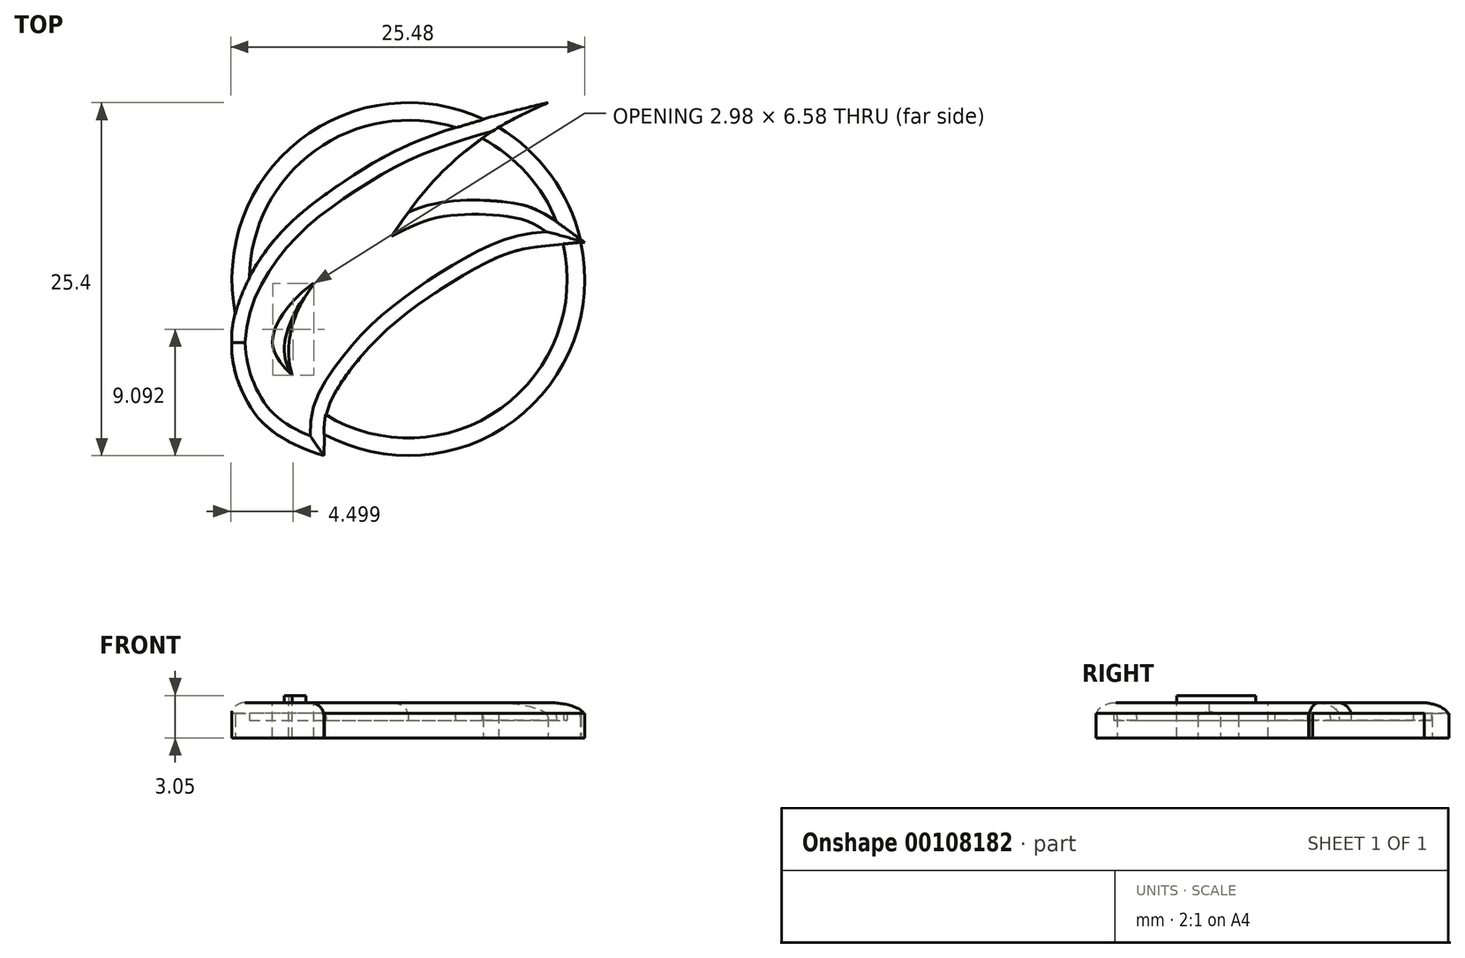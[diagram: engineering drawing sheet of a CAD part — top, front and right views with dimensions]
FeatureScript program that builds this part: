
annotation { "Feature Type Name" : "Feature", "Feature Type Description" : "" }
export const myFeature = defineFeature(function(context is Context, id is Id, definition is map)
    precondition{}
    {
        {
            var Q0;
            Q0=qCreatedBy(makeId("Top.planeOp"),FACE);
            var sketch = newSketch(context, id + "F0", { "sketchPlane" : qUnion([Q0])});
            skLineSegment(sketch, "E0.bottom", {"start": v(12.7, 12.7) * mm, "end": v(-12.7, 12.7) * mm});
            skLineSegment(sketch, "E0.top", {"start": v(12.7, -12.7) * mm, "end": v(-12.7, -12.7) * mm});
            skLineSegment(sketch, "E0.left", {"start": v(12.7, 12.7) * mm, "end": v(12.7, -12.7) * mm});
            skLineSegment(sketch, "E0.right", {"start": v(-12.7, 12.7) * mm, "end": v(-12.7, -12.7) * mm});
            skPoint(sketch, "E0.middle", {"position": v(0, 0) * mm});
            skFitSpline(sketch, "E1", {"points": [v(-6.08, -12.7) * mm, v(-11.49, -9) * mm, v(-12.7, -3.76) * mm, v(-9.57, 2.9) * mm, v(-4.09, 7.38) * mm, v(10.05, 12.7) * mm], "startDerivative": vector(-51.73, 16.39) * mm, "endDerivative": vector(97.1, 22.66) * mm});
            skFitSpline(sketch, "E2", {"points": [v(0, 4.8) * mm, v(6.97, 5.55) * mm, v(12.7, 2.64) * mm], "startDerivative": vector(12.66, 6.1) * mm, "endDerivative": vector(18.75, -14.7) * mm});
            skFitSpline(sketch, "E3", {"points": [v(-6.08, -12.7) * mm, v(-5.75, -9.17) * mm, v(-2.84, -4.93) * mm, v(1.65, -1.18) * mm, v(6.8, 1.73) * mm, v(12.7, 2.64) * mm], "startDerivative": vector(1.52, 34.14) * mm, "endDerivative": vector(48.68, 4.54) * mm});
            skFitSpline(sketch, "E4", {"points": [v(0, 4.8) * mm, v(4.64, 9.63) * mm, v(10.05, 12.7) * mm], "startDerivative": vector(11.2, 15.67) * mm, "endDerivative": vector(20.33, 9.14) * mm});
            skSolve(sketch);
        }
        {
            var Q0;
            {var subQ0=sQuery(id+"F0.wireOp",EDGE,"E1");var subQ1=sQuery(id+"F0.wireOp",EDGE,"E0.right");var subQ2=makeQuery(id+"F0.imprint","INTERSECT",VERTEX,{"disambiguationData":[OD(0.0)],"derivedFrom":[subQ1,subQ0]});Q0=makeQuery(id+"F0.imprint","IMPRINT",FACE,{"disambiguationData":[TD([[makeQuery(id+"F0.imprint","IMPRINT",EDGE,{"disambiguationData":[TD([[subQ2,-1.0]])],"derivedFrom":subQ1}),-1.0]])]});}
            var Q1;
            {var subQ0=sQuery(id+"F0.wireOp",EDGE,"c1Eb6WPf-WvlZ-wcMs-vn4g-5d7YpBRqAoRS");Q1=makeQuery(id+"F0.imprint","IMPRINT",FACE,{"disambiguationData":[TD([[makeQuery(id+"F0.imprint","IMPRINT",EDGE,{"derivedFrom":subQ0}),-1.0]])]});}
            var Q2;
            Q2=makeQuery(id+"F0.imprint","IMPRINT",FACE,{"disambiguationData":[TD([[makeQuery(id+"F0.imprint","IMPRINT",EDGE,{"derivedFrom":sQuery(id+"F0.wireOp",EDGE,"E2")}),-1.0]])]});
            extrude(context, id + "F1", {"entities" : qUnion([Q0, Q1, Q2]), "depth" : 2.54 * mm});
        }
        {
            var Q0;
            Q0=makeQuery(id+"F1.opExtrude","CAP_FACE",FACE,{"disambiguationData":[OSD([sQuery(id+"F0.wireOp",EDGE,"E1"),sQuery(id+"F0.wireOp",EDGE,"c1Eb6WPf-WvlZ-wcMs-vn4g-5d7YpBRqAoRS"),sQuery(id+"F0.wireOp",EDGE,"E2"),sQuery(id+"F0.wireOp",EDGE,"E3")])],"isStart":false});
            var sketch = newSketch(context, id + "F2", { "sketchPlane" : qUnion([Q0])});
            skFitSpline(sketch, "E5", {"points": [v(-6.8, -0.32) * mm, v(-9.75, -4.16) * mm, v(-8.37, -6.9) * mm], "startDerivative": vector(-5.92, -3.3) * mm, "endDerivative": vector(5.55, -5.41) * mm});
            skFitSpline(sketch, "E6", {"points": [v(-8.37, -6.9) * mm, v(-8.01, -2.38) * mm, v(-6.8, -0.32) * mm], "startDerivative": vector(-2.94, 9.89) * mm, "endDerivative": vector(4.93, 7.27) * mm});
            skSolve(sketch);
        }
        {
            var Q0;
            Q0=qCreatedBy(makeId("Top.planeOp"),FACE);
            var sketch = newSketch(context, id + "F3", { "sketchPlane" : qUnion([Q0])});
            skCircle(sketch, "E7", {"center": v(0, 0) * mm, "radius": 12.7 * mm});
            skSolve(sketch);
        }
        {
            var Q0;
            Q0 = qSketchRegion(id + "F3", true);
            extrude(context, id + "F4", {"entities" : qUnion([Q0]), "operationType" : NewBodyOperationType.ADD, "depth" : 1.27 * mm});
        }
        {
            var Q0;
            Q0 = qSketchRegion(id + "F2", true);
            extrude(context, id + "F5", {"entities" : qUnion([Q0]), "operationType" : NewBodyOperationType.REMOVE, "oppositeDirection" : true, "depth" : 25.4 * mm});
        }
        {
            var Q0;
            Q0=makeQuery(id+"F1.opExtrude","CAP_FACE",FACE,{"disambiguationData":[OSD([sQuery(id+"F0.wireOp",EDGE,"E1"),sQuery(id+"F0.wireOp",EDGE,"c1Eb6WPf-WvlZ-wcMs-vn4g-5d7YpBRqAoRS"),sQuery(id+"F0.wireOp",EDGE,"E2"),sQuery(id+"F0.wireOp",EDGE,"E3")])],"isStart":false});
            var sketch = newSketch(context, id + "F6", { "sketchPlane" : qUnion([Q0])});
            skFitSpline(sketch, "E8.0.0", {"points": [v(7.91, 12.7) * mm, v(4.26, 10.89) * mm, v(-2.84, 7.4) * mm, v(-8.76, 3.35) * mm, v(-14.41, -4.34) * mm, v(-9.73, -11.02) * mm, v(-6.67, -11.7) * mm, v(-3.5, -12.7) * mm]});
            skFitSpline(sketch, "E8.0.1", {"points": [v(-3.5, -12.7) * mm, v(-4.54, -10.95) * mm, v(-4.91, -10.68) * mm, v(-4.48, -6.55) * mm, v(-0.85, -3.27) * mm, v(6.87, 2.24) * mm, v(11.13, 6.28) * mm, v(12.7, 8.06) * mm]});
            skFitSpline(sketch, "E8.0.2", {"points": [v(12.7, 8.06) * mm, v(10.6, 7.69) * mm, v(6.36, 5.46) * mm, v(2.13, 3.93) * mm, v(0, 2.9) * mm]});
            skLineSegment(sketch, "E8.0.3", {"start": v(0, 4.8) * mm, "end": v(10.05, 12.7) * mm});
            skFitSpline(sketch, "E9.0", {"points": [v(-8.37, -6.9) * mm, v(-8.94, -5) * mm, v(-8.04, -2.15) * mm, v(-7.48, -1.34) * mm, v(-6.8, -0.32) * mm]});
            skFitSpline(sketch, "E10.0", {"points": [v(-6.8, -0.32) * mm, v(-7.9, -0.93) * mm, v(-10.85, -4.23) * mm, v(-9.19, -6.1) * mm, v(-8.37, -6.9) * mm]});
            skFitSpline(sketch, "E11", {"points": [v(-5.02, 1.46) * mm, v(-9.24, -1.15) * mm, v(-10.6, -3.67) * mm, v(-9.96, -6.28) * mm, v(-7.46, -8.48) * mm], "startDerivative": vector(-10.92, -6.69) * mm, "endDerivative": vector(10.93, -7.63) * mm});
            skFitSpline(sketch, "E12", {"points": [v(-7.46, -8.48) * mm, v(-7.79, -6.63) * mm, v(-7.8, -4.7) * mm, v(-7.11, -2.08) * mm, v(-5.02, 1.46) * mm], "startDerivative": vector(-1.8, 8.68) * mm, "endDerivative": vector(7.6, 11.4) * mm});
            skSolve(sketch);
        }
        {
            var Q0;
            Q0=makeQuery(id+"F6.imprint","IMPRINT",FACE,{"disambiguationData":[TD([[makeQuery(id+"F6.imprint","IMPRINT",EDGE,{"derivedFrom":sQuery(id+"F6.wireOp",EDGE,"E9.0")}),-1.0]])]});
            extrude(context, id + "F7", {"entities" : qUnion([Q0]), "operationType" : NewBodyOperationType.ADD, "depth" : 0.5 * mm});
        }
        {
            var Q0;
            Q0=makeQuery(id+"F1.opExtrude","CAP_EDGE",EDGE,{"disambiguationData":[OSD([sQuery(id+"F0.wireOp",EDGE,"c1Eb6WPf-WvlZ-wcMs-vn4g-5d7YpBRqAoRS")])],"isStart":false});
            var Q1;
            Q1=makeQuery(id+"F1.opExtrude","CAP_EDGE",EDGE,{"disambiguationData":[OSD([sQuery(id+"F0.wireOp",EDGE,"E1")])],"isStart":false});
            var Q2;
            Q2=makeQuery(id+"F1.opExtrude","CAP_EDGE",EDGE,{"disambiguationData":[OSD([sQuery(id+"F0.wireOp",EDGE,"E3")])],"isStart":false});
            var Q3;
            Q3=makeQuery(id+"F1.opExtrude","CAP_EDGE",EDGE,{"disambiguationData":[OSD([sQuery(id+"F0.wireOp",EDGE,"E2")])],"isStart":false});
            var Q4;
            {var subQ0=sQuery(id+"F3.wireOp",EDGE,"E7");Q4=makeQuery(id+"F4.boolean.opBoolean","SPLIT",EDGE,{"disambiguationData":[TD([makeQuery(id+"F1.opExtrude","SWEPT_FACE",FACE,{"disambiguationData":[OSD([sQuery(id+"F0.wireOp",EDGE,"c1Eb6WPf-WvlZ-wcMs-vn4g-5d7YpBRqAoRS")])]})])],"derivedFrom":makeQuery(id+"F4.opExtrude","CAP_EDGE",EDGE,{"disambiguationData":[OSD([subQ0])],"isStart":false})});}
            fillet(context, id + "F8", {"entities" : qUnion([Q0, Q1, Q2, Q3, Q4]), "radius" : 1.02 * mm, "tangentPropagation" : true, "allowEdgeOverflow" : false});
        }
        {
            var Q0;
            Q0=qCreatedBy(makeId("Top.planeOp"),FACE);
            var sketch = newSketch(context, id + "F9", { "sketchPlane" : qUnion([Q0])});
            skCircle(sketch, "E13", {"center": v(0, 0) * mm, "radius": 12.7 * mm});
            skCircle(sketch, "E14", {"center": v(0, 0) * mm, "radius": 11.43 * mm});
            skSolve(sketch);
        }
        {
            var Q0;
            Q0 = qSketchRegion(id + "F9", true);
            extrude(context, id + "F10", {"entities" : qUnion([Q0]), "operationType" : NewBodyOperationType.ADD, "depth" : 1.78 * mm});
        }
    });
